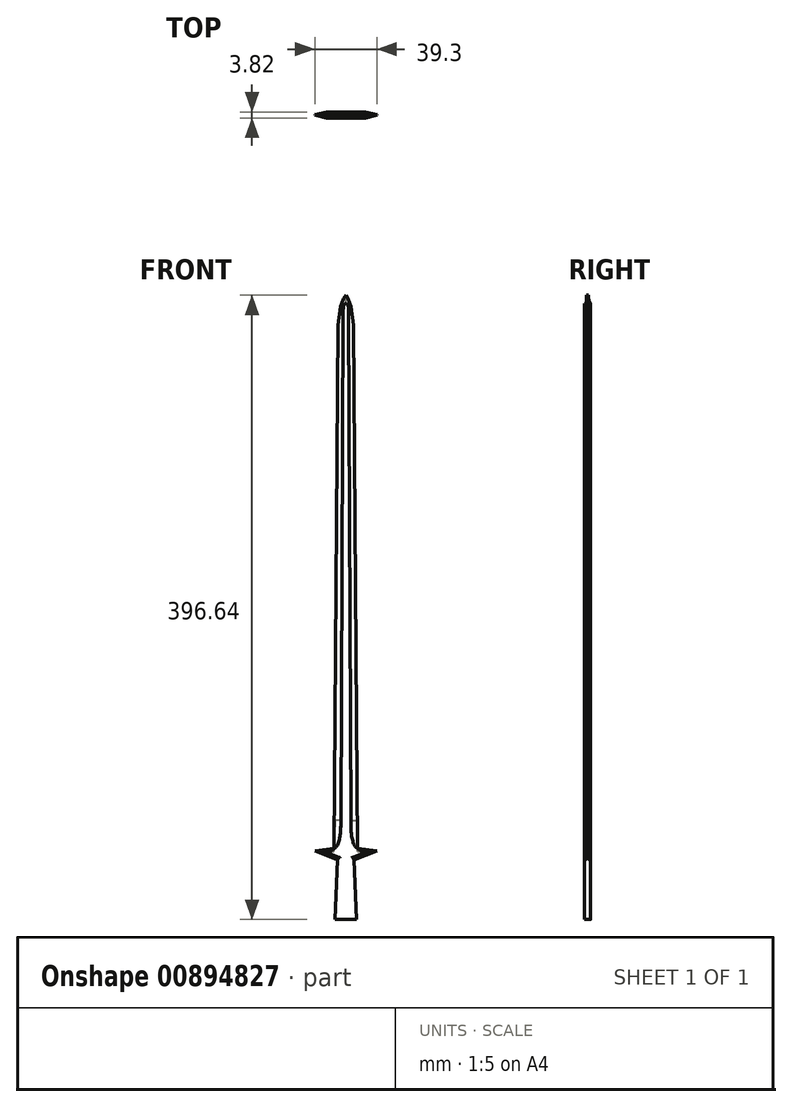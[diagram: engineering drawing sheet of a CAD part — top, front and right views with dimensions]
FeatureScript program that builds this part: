
annotation { "Feature Type Name" : "Feature", "Feature Type Description" : "" }
export const myFeature = defineFeature(function(context is Context, id is Id, definition is map)
    precondition{}
    {
        {
            var Q0;
            Q0=qCreatedBy(makeId("Front.planeOp"),FACE);
            var sketch = newSketch(context, id + "F0", { "sketchPlane" : qUnion([Q0])});
            skLineSegment(sketch, "E0", {"start": v(-6.84, 3.65) * mm, "end": v(-5.26, 41.69) * mm});
            skLineSegment(sketch, "E1", {"start": v(-5.26, 41.69) * mm, "end": v(-19.65, 47.2) * mm});
            skLineSegment(sketch, "E2", {"start": v(-19.65, 47.2) * mm, "end": v(-7.43, 48.78) * mm});
            skLineSegment(sketch, "E3", {"start": v(-7.43, 48.78) * mm, "end": v(-4.9, 381.3) * mm});
            skLineSegment(sketch, "E4", {"start": v(-4.9, 381.3) * mm, "end": v(-3.37, 393.1) * mm});
            skLineSegment(sketch, "E5", {"start": v(-3.37, 393.1) * mm, "end": v(-1.4, 398.2) * mm});
            skLineSegment(sketch, "E6.MirrorCS", {"start": v(6.84, 3.65) * mm, "end": v(5.26, 41.69) * mm});
            skLineSegment(sketch, "E7.MirrorCS", {"start": v(5.26, 41.69) * mm, "end": v(19.65, 47.2) * mm});
            skLineSegment(sketch, "E8.MirrorCS", {"start": v(19.65, 47.2) * mm, "end": v(7.43, 48.78) * mm});
            skLineSegment(sketch, "E9.MirrorCS", {"start": v(7.43, 48.78) * mm, "end": v(4.9, 381.3) * mm});
            skLineSegment(sketch, "E10.MirrorCS", {"start": v(4.9, 381.3) * mm, "end": v(3.37, 393.1) * mm});
            skLineSegment(sketch, "E11.MirrorCS", {"start": v(3.37, 393.1) * mm, "end": v(1.4, 398.2) * mm});
            skLineSegment(sketch, "E12", {"start": v(-1.4, 398.2) * mm, "end": v(0, 400.29) * mm});
            skLineSegment(sketch, "E13", {"start": v(0, 400.29) * mm, "end": v(1.4, 398.2) * mm});
            skLineSegment(sketch, "E14", {"start": v(-6.84, 3.65) * mm, "end": v(6.84, 3.65) * mm});
            skSolve(sketch);
        }
        {
            var Q0;
            Q0=makeQuery(id+"F0.imprint","IMPRINT",FACE,{"disambiguationData":[TD([[makeQuery(id+"F0.imprint","IMPRINT",EDGE,{"derivedFrom":sQuery(id+"F0.wireOp",EDGE,"E0")}),-1.0]])]});
            extrude(context, id + "F1", {"entities" : qUnion([Q0]), "depth" : 0.64 * mm, "offsetDistance" : 25.4 * mm});
        }
        {
            var Q0;
            Q0=makeQuery(id+"F1.opExtrude","CAP_FACE",FACE,{"disambiguationData":[OSD([sQuery(id+"F0.wireOp",EDGE,"E0"),sQuery(id+"F0.wireOp",EDGE,"E1"),sQuery(id+"F0.wireOp",EDGE,"E2"),sQuery(id+"F0.wireOp",EDGE,"E3"),sQuery(id+"F0.wireOp",EDGE,"E4"),sQuery(id+"F0.wireOp",EDGE,"E5"),sQuery(id+"F0.wireOp",EDGE,"E6.MirrorCS"),sQuery(id+"F0.wireOp",EDGE,"E7.MirrorCS"),sQuery(id+"F0.wireOp",EDGE,"E8.MirrorCS"),sQuery(id+"F0.wireOp",EDGE,"E9.MirrorCS"),sQuery(id+"F0.wireOp",EDGE,"E10.MirrorCS"),sQuery(id+"F0.wireOp",EDGE,"E11.MirrorCS"),sQuery(id+"F0.wireOp",EDGE,"E12"),sQuery(id+"F0.wireOp",EDGE,"E13"),sQuery(id+"F0.wireOp",EDGE,"E14")])],"isStart":true});
            extrude(context, id + "F2", {"entities" : qUnion([Q0]), "operationType" : NewBodyOperationType.ADD, "depth" : 0.64 * mm, "offsetDistance" : 25.4 * mm});
        }
        {
            var Q0;
            Q0=makeQuery(id+"F1.opExtrude","CAP_FACE",FACE,{"disambiguationData":[OSD([sQuery(id+"F0.wireOp",EDGE,"E0"),sQuery(id+"F0.wireOp",EDGE,"E1"),sQuery(id+"F0.wireOp",EDGE,"E2"),sQuery(id+"F0.wireOp",EDGE,"E3"),sQuery(id+"F0.wireOp",EDGE,"E4"),sQuery(id+"F0.wireOp",EDGE,"E5"),sQuery(id+"F0.wireOp",EDGE,"E6.MirrorCS"),sQuery(id+"F0.wireOp",EDGE,"E7.MirrorCS"),sQuery(id+"F0.wireOp",EDGE,"E8.MirrorCS"),sQuery(id+"F0.wireOp",EDGE,"E9.MirrorCS"),sQuery(id+"F0.wireOp",EDGE,"E10.MirrorCS"),sQuery(id+"F0.wireOp",EDGE,"E11.MirrorCS"),sQuery(id+"F0.wireOp",EDGE,"E12"),sQuery(id+"F0.wireOp",EDGE,"E13"),sQuery(id+"F0.wireOp",EDGE,"E14")])],"isStart":false});
            var sketch = newSketch(context, id + "F3", { "sketchPlane" : qUnion([Q0])});
            skFitSpline(sketch, "E15", {"points": [v(-7.43, 48.78) * mm, v(-5.84, 50.08) * mm, v(-4.65, 52.63) * mm, v(-3.8, 56.07) * mm, v(-3.37, 59.46) * mm, v(-3.2, 66.68) * mm], "startDerivative": vector(11.35, 7.4) * mm, "endDerivative": vector(0.22, 28.16) * mm});
            skLineSegment(sketch, "E16", {"start": v(-3.2, 66.68) * mm, "end": v(-1.69, 387.82) * mm});
            skFitSpline(sketch, "E17", {"points": [v(-1.69, 387.82) * mm, v(-1.69, 391.15) * mm, v(-1.1, 394.16) * mm, v(0, 395.07) * mm], "startDerivative": vector(-0.21, 8.48) * mm, "endDerivative": vector(4.9, 2.68) * mm});
            skLineSegment(sketch, "E18", {"start": v(0, 395.07) * mm, "end": v(0, 389.98) * mm});
            skFitSpline(sketch, "E19.MirrorCS", {"points": [v(1.69, 387.82) * mm, v(1.69, 391.15) * mm, v(1.1, 394.16) * mm, v(0, 395.07) * mm], "startDerivative": vector(0.21, 8.48) * mm, "endDerivative": vector(-4.9, 2.68) * mm});
            skLineSegment(sketch, "E20.MirrorCS", {"start": v(3.2, 66.68) * mm, "end": v(1.69, 387.82) * mm});
            skFitSpline(sketch, "E21.MirrorCS", {"points": [v(7.43, 48.78) * mm, v(5.84, 50.08) * mm, v(4.65, 52.63) * mm, v(3.8, 56.07) * mm, v(3.37, 59.46) * mm, v(3.2, 66.68) * mm], "startDerivative": vector(-11.35, 7.4) * mm, "endDerivative": vector(-0.22, 28.16) * mm});
            skSolve(sketch);
        }
        {
            var Q0;
            Q0=makeQuery(id+"F3.imprint","IMPRINT",FACE,{"disambiguationData":[TD([[makeQuery(id+"F3.imprint","IMPRINT",EDGE,{"derivedFrom":sQuery(id+"F3.wireOp",EDGE,"E15")}),-1.0]])]});
            extrude(context, id + "F4", {"entities" : qUnion([Q0]), "operationType" : NewBodyOperationType.ADD, "depth" : 1.27 * mm, "offsetDistance" : 25.4 * mm});
        }
        {
            var Q0;
            Q0=makeQuery(id+"F4.opExtrude","CAP_FACE",FACE,{"disambiguationData":[OSD([sQuery(id+"F0.wireOp",EDGE,"E0"),sQuery(id+"F0.wireOp",EDGE,"E1"),sQuery(id+"F0.wireOp",EDGE,"E2"),sQuery(id+"F0.wireOp",EDGE,"E6.MirrorCS"),sQuery(id+"F0.wireOp",EDGE,"E7.MirrorCS"),sQuery(id+"F0.wireOp",EDGE,"E8.MirrorCS"),sQuery(id+"F0.wireOp",EDGE,"E14"),sQuery(id+"F3.wireOp",EDGE,"E15"),sQuery(id+"F3.wireOp",EDGE,"E16"),sQuery(id+"F3.wireOp",EDGE,"E17"),sQuery(id+"F3.wireOp",EDGE,"E19.MirrorCS"),sQuery(id+"F3.wireOp",EDGE,"E20.MirrorCS"),sQuery(id+"F3.wireOp",EDGE,"E21.MirrorCS")])],"isStart":false});
            extrude(context, id + "F5", {"entities" : qUnion([Q0]), "operationType" : NewBodyOperationType.ADD, "oppositeDirection" : true, "depth" : 3.8 * mm, "offsetDistance" : 25.4 * mm});
        }
        {
            var Q0;
            Q0=makeQuery(id+"F4.opExtrude","CAP_EDGE",EDGE,{"disambiguationData":[OSD([sQuery(id+"F3.wireOp",EDGE,"E15")])],"isStart":true});
            var Q1;
            Q1=makeQuery(id+"F4.opExtrude","CAP_EDGE",EDGE,{"disambiguationData":[OSD([sQuery(id+"F3.wireOp",EDGE,"E21.MirrorCS")])],"isStart":true});
            var Q2;
            Q2=makeQuery(id+"F4.opExtrude","CAP_EDGE",EDGE,{"disambiguationData":[OSD([sQuery(id+"F3.wireOp",EDGE,"E20.MirrorCS")])],"isStart":true});
            var Q3;
            Q3=makeQuery(id+"F4.opExtrude","CAP_EDGE",EDGE,{"disambiguationData":[OSD([sQuery(id+"F3.wireOp",EDGE,"E16")])],"isStart":true});
            var Q4;
            Q4=makeQuery(id+"F4.opExtrude","CAP_EDGE",EDGE,{"disambiguationData":[OSD([sQuery(id+"F3.wireOp",EDGE,"E17")])],"isStart":true});
            var Q5;
            Q5=makeQuery(id+"F4.opExtrude","CAP_EDGE",EDGE,{"disambiguationData":[OSD([sQuery(id+"F3.wireOp",EDGE,"E19.MirrorCS")])],"isStart":true});
            var Q6;
            Q6=makeQuery(id+"F5.boolean.opBoolean","INTERSECT",EDGE,{"derivedFrom":[makeQuery(id+"F2.opExtrude","CAP_FACE",FACE,{"disambiguationData":[OSD([sQuery(id+"F0.wireOp",EDGE,"E0"),sQuery(id+"F0.wireOp",EDGE,"E1"),sQuery(id+"F0.wireOp",EDGE,"E2"),sQuery(id+"F0.wireOp",EDGE,"E3"),sQuery(id+"F0.wireOp",EDGE,"E4"),sQuery(id+"F0.wireOp",EDGE,"E5"),sQuery(id+"F0.wireOp",EDGE,"E6.MirrorCS"),sQuery(id+"F0.wireOp",EDGE,"E7.MirrorCS"),sQuery(id+"F0.wireOp",EDGE,"E8.MirrorCS"),sQuery(id+"F0.wireOp",EDGE,"E9.MirrorCS"),sQuery(id+"F0.wireOp",EDGE,"E10.MirrorCS"),sQuery(id+"F0.wireOp",EDGE,"E11.MirrorCS"),sQuery(id+"F0.wireOp",EDGE,"E12"),sQuery(id+"F0.wireOp",EDGE,"E13"),sQuery(id+"F0.wireOp",EDGE,"E14")])],"isStart":false}),makeQuery(id+"F5.opExtrude","SWEPT_FACE",FACE,{"disambiguationData":[OSD([sQuery(id+"F3.wireOp",EDGE,"E17")])]})]});
            var Q7;
            Q7=makeQuery(id+"F5.boolean.opBoolean","INTERSECT",EDGE,{"derivedFrom":[makeQuery(id+"F2.opExtrude","CAP_FACE",FACE,{"disambiguationData":[OSD([sQuery(id+"F0.wireOp",EDGE,"E0"),sQuery(id+"F0.wireOp",EDGE,"E1"),sQuery(id+"F0.wireOp",EDGE,"E2"),sQuery(id+"F0.wireOp",EDGE,"E3"),sQuery(id+"F0.wireOp",EDGE,"E4"),sQuery(id+"F0.wireOp",EDGE,"E5"),sQuery(id+"F0.wireOp",EDGE,"E6.MirrorCS"),sQuery(id+"F0.wireOp",EDGE,"E7.MirrorCS"),sQuery(id+"F0.wireOp",EDGE,"E8.MirrorCS"),sQuery(id+"F0.wireOp",EDGE,"E9.MirrorCS"),sQuery(id+"F0.wireOp",EDGE,"E10.MirrorCS"),sQuery(id+"F0.wireOp",EDGE,"E11.MirrorCS"),sQuery(id+"F0.wireOp",EDGE,"E12"),sQuery(id+"F0.wireOp",EDGE,"E13"),sQuery(id+"F0.wireOp",EDGE,"E14")])],"isStart":false}),makeQuery(id+"F5.opExtrude","SWEPT_FACE",FACE,{"disambiguationData":[OSD([sQuery(id+"F3.wireOp",EDGE,"E19.MirrorCS")])]})]});
            var Q8;
            Q8=makeQuery(id+"F5.boolean.opBoolean","INTERSECT",EDGE,{"derivedFrom":[makeQuery(id+"F2.opExtrude","CAP_FACE",FACE,{"disambiguationData":[OSD([sQuery(id+"F0.wireOp",EDGE,"E0"),sQuery(id+"F0.wireOp",EDGE,"E1"),sQuery(id+"F0.wireOp",EDGE,"E2"),sQuery(id+"F0.wireOp",EDGE,"E3"),sQuery(id+"F0.wireOp",EDGE,"E4"),sQuery(id+"F0.wireOp",EDGE,"E5"),sQuery(id+"F0.wireOp",EDGE,"E6.MirrorCS"),sQuery(id+"F0.wireOp",EDGE,"E7.MirrorCS"),sQuery(id+"F0.wireOp",EDGE,"E8.MirrorCS"),sQuery(id+"F0.wireOp",EDGE,"E9.MirrorCS"),sQuery(id+"F0.wireOp",EDGE,"E10.MirrorCS"),sQuery(id+"F0.wireOp",EDGE,"E11.MirrorCS"),sQuery(id+"F0.wireOp",EDGE,"E12"),sQuery(id+"F0.wireOp",EDGE,"E13"),sQuery(id+"F0.wireOp",EDGE,"E14")])],"isStart":false}),makeQuery(id+"F5.opExtrude","SWEPT_FACE",FACE,{"disambiguationData":[OSD([sQuery(id+"F3.wireOp",EDGE,"E20.MirrorCS")])]})]});
            var Q9;
            Q9=makeQuery(id+"F5.boolean.opBoolean","INTERSECT",EDGE,{"derivedFrom":[makeQuery(id+"F2.opExtrude","CAP_FACE",FACE,{"disambiguationData":[OSD([sQuery(id+"F0.wireOp",EDGE,"E0"),sQuery(id+"F0.wireOp",EDGE,"E1"),sQuery(id+"F0.wireOp",EDGE,"E2"),sQuery(id+"F0.wireOp",EDGE,"E3"),sQuery(id+"F0.wireOp",EDGE,"E4"),sQuery(id+"F0.wireOp",EDGE,"E5"),sQuery(id+"F0.wireOp",EDGE,"E6.MirrorCS"),sQuery(id+"F0.wireOp",EDGE,"E7.MirrorCS"),sQuery(id+"F0.wireOp",EDGE,"E8.MirrorCS"),sQuery(id+"F0.wireOp",EDGE,"E9.MirrorCS"),sQuery(id+"F0.wireOp",EDGE,"E10.MirrorCS"),sQuery(id+"F0.wireOp",EDGE,"E11.MirrorCS"),sQuery(id+"F0.wireOp",EDGE,"E12"),sQuery(id+"F0.wireOp",EDGE,"E13"),sQuery(id+"F0.wireOp",EDGE,"E14")])],"isStart":false}),makeQuery(id+"F5.opExtrude","SWEPT_FACE",FACE,{"disambiguationData":[OSD([sQuery(id+"F3.wireOp",EDGE,"E16")])]})]});
            var Q10;
            Q10=makeQuery(id+"F5.boolean.opBoolean","INTERSECT",EDGE,{"derivedFrom":[makeQuery(id+"F2.opExtrude","CAP_FACE",FACE,{"disambiguationData":[OSD([sQuery(id+"F0.wireOp",EDGE,"E0"),sQuery(id+"F0.wireOp",EDGE,"E1"),sQuery(id+"F0.wireOp",EDGE,"E2"),sQuery(id+"F0.wireOp",EDGE,"E3"),sQuery(id+"F0.wireOp",EDGE,"E4"),sQuery(id+"F0.wireOp",EDGE,"E5"),sQuery(id+"F0.wireOp",EDGE,"E6.MirrorCS"),sQuery(id+"F0.wireOp",EDGE,"E7.MirrorCS"),sQuery(id+"F0.wireOp",EDGE,"E8.MirrorCS"),sQuery(id+"F0.wireOp",EDGE,"E9.MirrorCS"),sQuery(id+"F0.wireOp",EDGE,"E10.MirrorCS"),sQuery(id+"F0.wireOp",EDGE,"E11.MirrorCS"),sQuery(id+"F0.wireOp",EDGE,"E12"),sQuery(id+"F0.wireOp",EDGE,"E13"),sQuery(id+"F0.wireOp",EDGE,"E14")])],"isStart":false}),makeQuery(id+"F5.opExtrude","SWEPT_FACE",FACE,{"disambiguationData":[OSD([sQuery(id+"F3.wireOp",EDGE,"E15")])]})]});
            var Q11;
            Q11=makeQuery(id+"F5.boolean.opBoolean","INTERSECT",EDGE,{"derivedFrom":[makeQuery(id+"F2.opExtrude","CAP_FACE",FACE,{"disambiguationData":[OSD([sQuery(id+"F0.wireOp",EDGE,"E0"),sQuery(id+"F0.wireOp",EDGE,"E1"),sQuery(id+"F0.wireOp",EDGE,"E2"),sQuery(id+"F0.wireOp",EDGE,"E3"),sQuery(id+"F0.wireOp",EDGE,"E4"),sQuery(id+"F0.wireOp",EDGE,"E5"),sQuery(id+"F0.wireOp",EDGE,"E6.MirrorCS"),sQuery(id+"F0.wireOp",EDGE,"E7.MirrorCS"),sQuery(id+"F0.wireOp",EDGE,"E8.MirrorCS"),sQuery(id+"F0.wireOp",EDGE,"E9.MirrorCS"),sQuery(id+"F0.wireOp",EDGE,"E10.MirrorCS"),sQuery(id+"F0.wireOp",EDGE,"E11.MirrorCS"),sQuery(id+"F0.wireOp",EDGE,"E12"),sQuery(id+"F0.wireOp",EDGE,"E13"),sQuery(id+"F0.wireOp",EDGE,"E14")])],"isStart":false}),makeQuery(id+"F5.opExtrude","SWEPT_FACE",FACE,{"disambiguationData":[OSD([sQuery(id+"F3.wireOp",EDGE,"E21.MirrorCS")])]})]});
            fillet(context, id + "F6", {"entities" : qUnion([Q0, Q1, Q2, Q3, Q4, Q5, Q6, Q7, Q8, Q9, Q10, Q11]), "radius" : 6.35 * mm, "tangentPropagation" : true, "allowEdgeOverflow" : false});
        }
        {
            var Q0;
            Q0=makeQuery(id+"F5.opExtrude","CAP_EDGE",EDGE,{"disambiguationData":[OSD([sQuery(id+"F0.wireOp",EDGE,"E8.MirrorCS")])],"isStart":false});
            var Q1;
            Q1=makeQuery(id+"F5.opExtrude","CAP_EDGE",EDGE,{"disambiguationData":[OSD([sQuery(id+"F0.wireOp",EDGE,"E2")])],"isStart":false});
            var Q2;
            Q2=makeQuery(id+"F5.opExtrude","CAP_EDGE",EDGE,{"disambiguationData":[OSD([sQuery(id+"F0.wireOp",EDGE,"E1")])],"isStart":false});
            var Q3;
            Q3=makeQuery(id+"F5.opExtrude","CAP_EDGE",EDGE,{"disambiguationData":[OSD([sQuery(id+"F0.wireOp",EDGE,"E7.MirrorCS")])],"isStart":false});
            var Q4;
            Q4=makeQuery(id+"F4.opExtrude","CAP_EDGE",EDGE,{"disambiguationData":[OSD([sQuery(id+"F0.wireOp",EDGE,"E8.MirrorCS")])],"isStart":false});
            var Q5;
            Q5=makeQuery(id+"F4.opExtrude","CAP_EDGE",EDGE,{"disambiguationData":[OSD([sQuery(id+"F0.wireOp",EDGE,"E7.MirrorCS")])],"isStart":false});
            var Q6;
            Q6=makeQuery(id+"F4.opExtrude","CAP_EDGE",EDGE,{"disambiguationData":[OSD([sQuery(id+"F0.wireOp",EDGE,"E1")])],"isStart":false});
            var Q7;
            Q7=makeQuery(id+"F4.opExtrude","CAP_EDGE",EDGE,{"disambiguationData":[OSD([sQuery(id+"F0.wireOp",EDGE,"E2")])],"isStart":false});
            chamfer(context, id + "F7", {"entities" : qUnion([Q0, Q1, Q2, Q3, Q4, Q5, Q6, Q7]), "width" : 1.78 * mm, "tangentPropagation" : true});
        }
        {
            var Q0;
            Q0=makeQuery(id+"F4.opExtrude","CAP_EDGE",EDGE,{"disambiguationData":[OSD([sQuery(id+"F0.wireOp",EDGE,"E6.MirrorCS")])],"isStart":false});
            var Q1;
            Q1=makeQuery(id+"F4.opExtrude","CAP_EDGE",EDGE,{"disambiguationData":[OSD([sQuery(id+"F0.wireOp",EDGE,"E0")])],"isStart":false});
            var Q2;
            Q2=makeQuery(id+"F5.opExtrude","CAP_EDGE",EDGE,{"disambiguationData":[OSD([sQuery(id+"F0.wireOp",EDGE,"E0")])],"isStart":false});
            var Q3;
            Q3=makeQuery(id+"F5.opExtrude","CAP_EDGE",EDGE,{"disambiguationData":[OSD([sQuery(id+"F0.wireOp",EDGE,"E6.MirrorCS")])],"isStart":false});
            fillet(context, id + "F8", {"entities" : qUnion([Q0, Q1, Q2, Q3]), "radius" : 1.52 * mm, "tangentPropagation" : true, "allowEdgeOverflow" : false});
        }
    });
